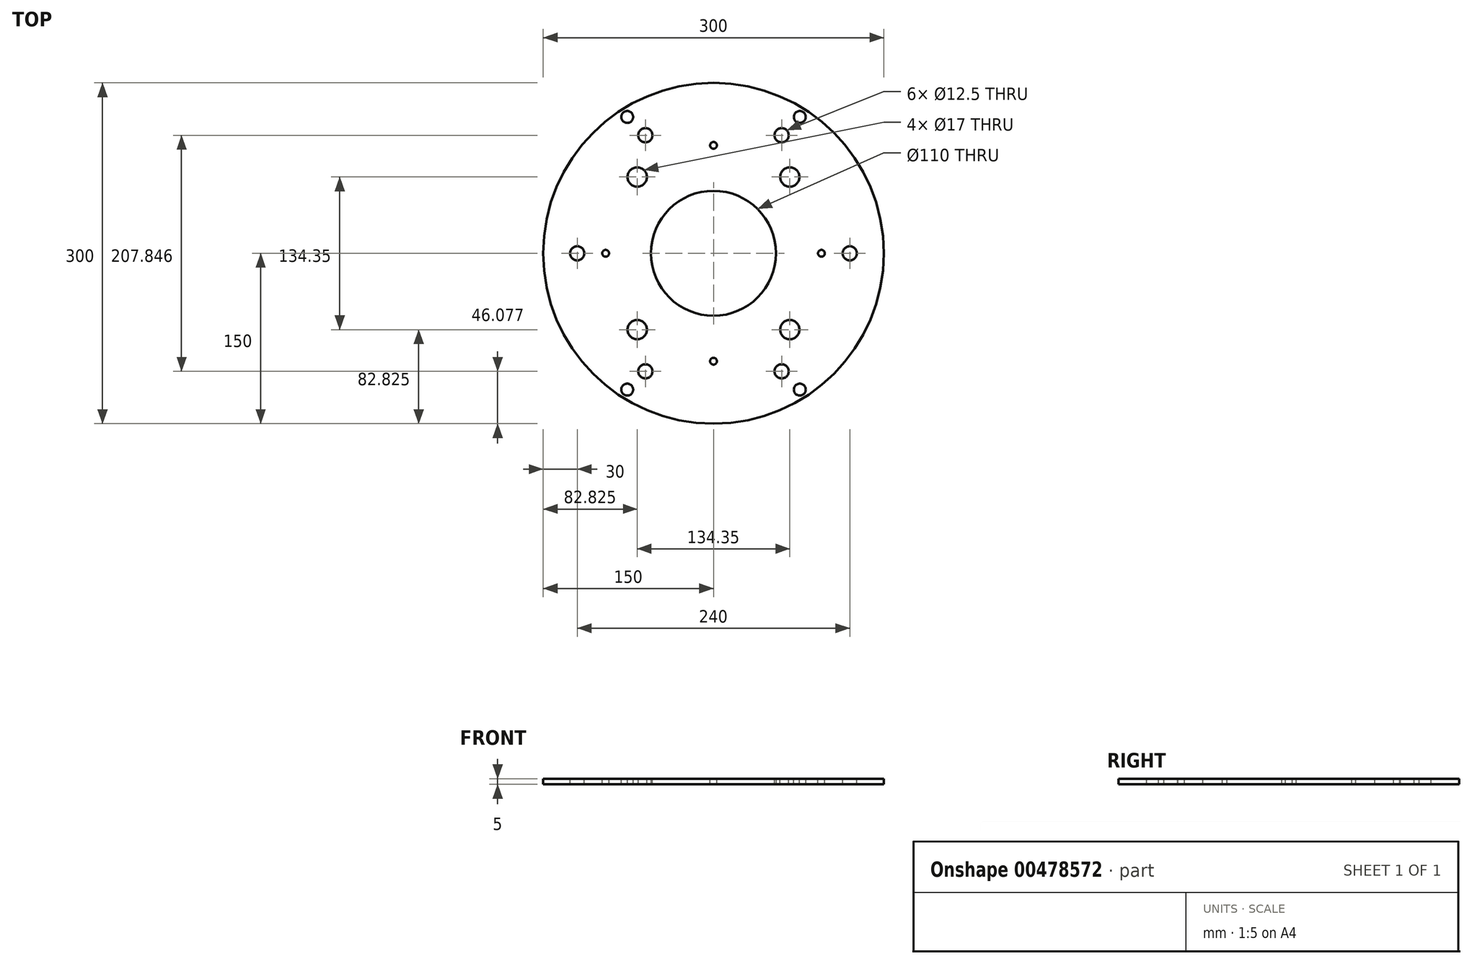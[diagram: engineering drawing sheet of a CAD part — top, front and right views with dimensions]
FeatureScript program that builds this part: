
annotation { "Feature Type Name" : "Feature", "Feature Type Description" : "" }
export const myFeature = defineFeature(function(context is Context, id is Id, definition is map)
    precondition{}
    {
        {
            var Q0;
            Q0=qCreatedBy(makeId("Right.planeOp"),FACE);
            var sketch = newSketch(context, id + "F0", { "sketchPlane" : qUnion([Q0])});
            skLineSegment(sketch, "E0", {"start": v(0, 0) * mm, "end": v(0, 175.97) * mm, "construction": true});
            skLineSegment(sketch, "E1.bottom", {"start": v(55, 0) * mm, "end": v(150, 0) * mm});
            skLineSegment(sketch, "E1.top", {"start": v(55, 5) * mm, "end": v(150, 5) * mm});
            skLineSegment(sketch, "E1.left", {"start": v(55, 0) * mm, "end": v(55, 5) * mm});
            skLineSegment(sketch, "E1.right", {"start": v(150, 0) * mm, "end": v(150, 5) * mm});
            skLineSegment(sketch, "E2.bottom", {"start": v(55, 5) * mm, "end": v(62.5, 5) * mm});
            skLineSegment(sketch, "E2.top", {"start": v(55, 125) * mm, "end": v(62.5, 125) * mm});
            skLineSegment(sketch, "E2.left", {"start": v(55, 5) * mm, "end": v(55, 125) * mm});
            skLineSegment(sketch, "E2.right", {"start": v(62.5, 5) * mm, "end": v(62.5, 125) * mm});
            skSolve(sketch);
        }
        {
            var Q0;
            Q0=makeQuery(id+"F0.imprint","IMPRINT",FACE,{"disambiguationData":[TD([[makeQuery(id+"F0.imprint","IMPRINT",EDGE,{"derivedFrom":sQuery(id+"F0.wireOp",EDGE,"E1.bottom")}),1.0]])]});
            var Q1;
            Q1=makeQuery(id+"F0.imprint","IMPRINT",FACE,{"disambiguationData":[TD([[makeQuery(id+"F0.imprint","IMPRINT",EDGE,{"derivedFrom":sQuery(id+"F0.wireOp",EDGE,"E2.bottom")}),1.0]])]});
            var Q2;
            Q2=sQuery(id+"F0.wireOp",EDGE,"E0");
            revolve(context, id + "F1", {"entities" : qUnion([Q0, Q1]), "axis" : qUnion([Q2]), "revolveType" : RevolveType.FULL});
        }
        {
            var Q0;
            Q0=makeQuery(id+"F1.opRevolve","SWEPT_FACE",FACE,{"disambiguationData":[OSD([sQuery(id+"F0.wireOp",EDGE,"E1.top")])]});
            var sketch = newSketch(context, id + "F2", { "sketchPlane" : qUnion([Q0])});
            skCircle(sketch, "E3", {"center": v(-120, 0) * mm, "radius": 6.25 * mm});
            skCircle(sketch, "E4.1.0", {"center": v(-60, -103.92) * mm, "radius": 6.25 * mm});
            skCircle(sketch, "E4.2.0", {"center": v(60, -103.92) * mm, "radius": 6.25 * mm});
            skPoint(sketch, "E4.center", {"position": v(0, 0) * mm});
            skCircle(sketch, "E5.1.3.0", {"center": v(120, 0) * mm, "radius": 6.25 * mm});
            skCircle(sketch, "E5.1.4.0", {"center": v(60, 103.92) * mm, "radius": 6.25 * mm});
            skCircle(sketch, "E5.1.5.0", {"center": v(-60, 103.92) * mm, "radius": 6.25 * mm});
            skCircle(sketch, "E6", {"center": v(0, 95) * mm, "radius": 3 * mm});
            skCircle(sketch, "E7.1.0", {"center": v(-95, 0) * mm, "radius": 3 * mm});
            skCircle(sketch, "E7.2.0", {"center": v(0, -95) * mm, "radius": 3 * mm});
            skCircle(sketch, "E7.3.0", {"center": v(95, 0) * mm, "radius": 3 * mm});
            skLineSegment(sketch, "E8", {"start": v(0, 0) * mm, "end": v(-118.07, 118.07) * mm, "construction": true});
            skCircle(sketch, "E9", {"center": v(0, 0) * mm, "radius": 95 * mm, "construction": true});
            skCircle(sketch, "E10", {"center": v(-67.18, 67.18) * mm, "radius": 8.5 * mm});
            skCircle(sketch, "E11.1.0", {"center": v(-67.18, -67.18) * mm, "radius": 8.5 * mm});
            skCircle(sketch, "E11.2.0", {"center": v(67.18, -67.18) * mm, "radius": 8.5 * mm});
            skCircle(sketch, "E12.1.3.0", {"center": v(67.18, 67.18) * mm, "radius": 8.5 * mm});
            skLineSegment(sketch, "E13", {"start": v(0, 0) * mm, "end": v(-60, 103.92) * mm, "construction": true});
            skCircle(sketch, "E14", {"center": v(-76, 120) * mm, "radius": 5.25 * mm});
            skCircle(sketch, "E15.0.1.0", {"center": v(-76, -120) * mm, "radius": 5.25 * mm});
            skCircle(sketch, "E15.1.0.0", {"center": v(76, 120) * mm, "radius": 5.25 * mm});
            skCircle(sketch, "E15.1.1.0", {"center": v(76, -120) * mm, "radius": 5.25 * mm});
            skLineSegment(sketch, "E15.direction1", {"start": v(-76, 120) * mm, "end": v(76, 120) * mm, "construction": true});
            skLineSegment(sketch, "E15.direction2", {"start": v(-76, 120) * mm, "end": v(-76, -120) * mm, "construction": true});
            skSolve(sketch);
        }
        {
            var Q0;
            Q0 = qSketchRegion(id + "F2", true);
            extrude(context, id + "F3", {"entities" : qUnion([Q0]), "operationType" : NewBodyOperationType.REMOVE, "endBound" : BoundingType.THROUGH_ALL, "oppositeDirection" : true, "depth" : 25 * mm, "offsetDistance" : 25 * mm});
        }
    });
